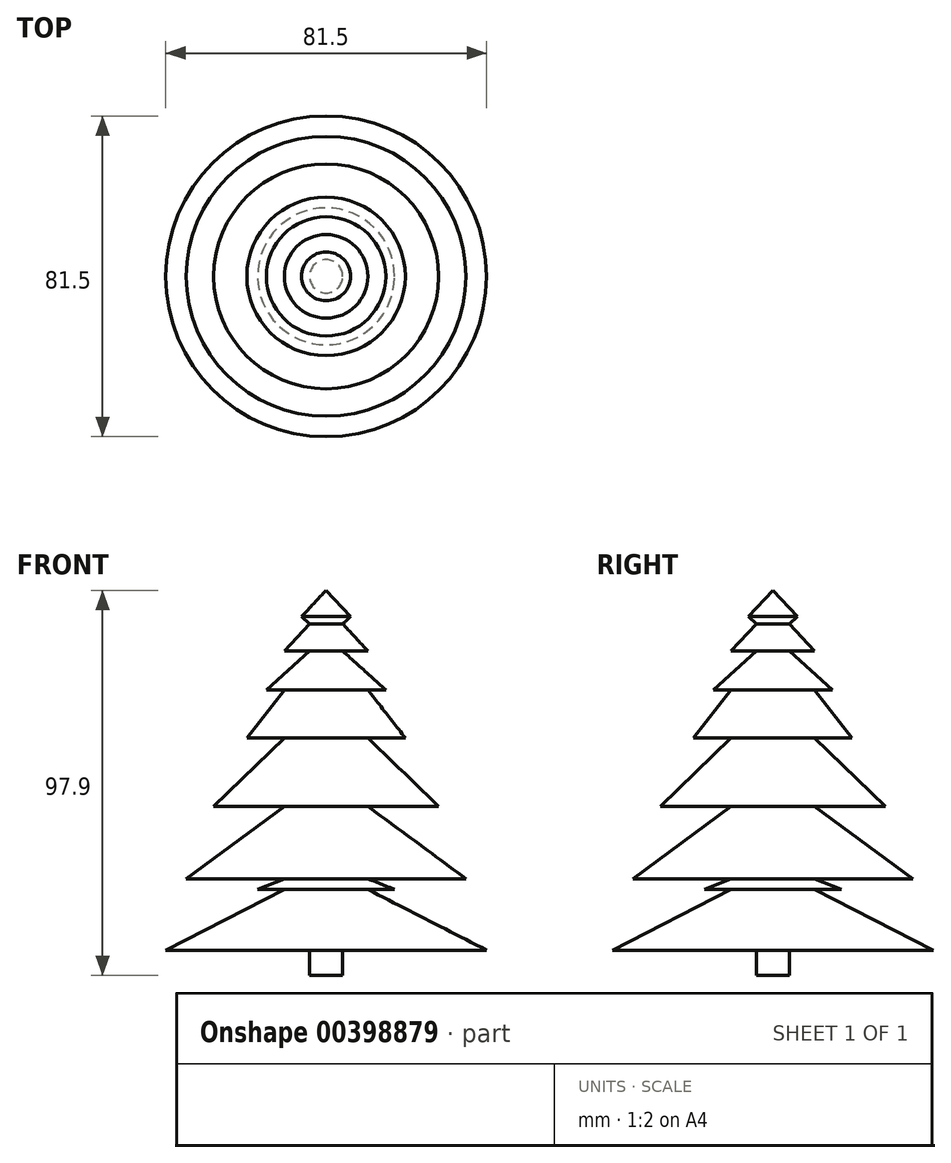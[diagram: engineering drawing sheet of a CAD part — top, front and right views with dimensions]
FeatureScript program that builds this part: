
annotation { "Feature Type Name" : "Feature", "Feature Type Description" : "" }
export const myFeature = defineFeature(function(context is Context, id is Id, definition is map)
    precondition{}
    {
        {
            var Q0;
            Q0=qCreatedBy(makeId("Front.planeOp"),FACE);
            var sketch = newSketch(context, id + "F0", { "sketchPlane" : qUnion([Q0])});
            skLineSegment(sketch, "E0", {"start": v(0, 59.14) * mm, "end": v(6.21, 52.43) * mm});
            skLineSegment(sketch, "E1", {"start": v(6.21, 52.43) * mm, "end": v(4.23, 50.59) * mm});
            skLineSegment(sketch, "E2", {"start": v(4.23, 50.59) * mm, "end": v(10.62, 43.69) * mm});
            skLineSegment(sketch, "E3", {"start": v(10.62, 43.69) * mm, "end": v(4.23, 43.69) * mm});
            skLineSegment(sketch, "E4", {"start": v(4.23, 43.69) * mm, "end": v(15.16, 33.8) * mm});
            skLineSegment(sketch, "E5", {"start": v(15.16, 33.8) * mm, "end": v(10.62, 33.8) * mm});
            skLineSegment(sketch, "E6", {"start": v(10.62, 33.8) * mm, "end": v(20.13, 21.62) * mm});
            skLineSegment(sketch, "E7", {"start": v(20.13, 21.62) * mm, "end": v(10.62, 21.62) * mm});
            skLineSegment(sketch, "E8", {"start": v(10.62, 21.62) * mm, "end": v(28.57, 4.22) * mm});
            skLineSegment(sketch, "E9", {"start": v(28.57, 4.22) * mm, "end": v(10.62, 4.22) * mm});
            skLineSegment(sketch, "E10", {"start": v(10.62, 4.22) * mm, "end": v(35.53, -14.16) * mm});
            skLineSegment(sketch, "E11", {"start": v(35.53, -14.16) * mm, "end": v(10.62, -14.16) * mm});
            skLineSegment(sketch, "E12", {"start": v(10.62, -14.16) * mm, "end": v(17.4, -16.9) * mm});
            skLineSegment(sketch, "E13", {"start": v(17.4, -16.9) * mm, "end": v(10.62, -16.9) * mm});
            skLineSegment(sketch, "E14", {"start": v(10.62, -16.9) * mm, "end": v(40.75, -32.3) * mm});
            skLineSegment(sketch, "E15", {"start": v(40.75, -32.3) * mm, "end": v(4.23, -32.3) * mm});
            skLineSegment(sketch, "E16", {"start": v(4.23, -32.3) * mm, "end": v(4.23, -38.76) * mm});
            skLineSegment(sketch, "E17", {"start": v(4.23, -38.76) * mm, "end": v(0, -38.76) * mm});
            skLineSegment(sketch, "E18", {"start": v(0, 59.14) * mm, "end": v(0, -38.76) * mm});
            skSolve(sketch);
        }
        {
            var Q0;
            Q0=makeQuery(id+"F0.imprint","IMPRINT",FACE,{"disambiguationData":[TD([[makeQuery(id+"F0.imprint","IMPRINT",EDGE,{"derivedFrom":sQuery(id+"F0.wireOp",EDGE,"E0")}),-1.0]])]});
            var Q1;
            Q1=sQuery(id+"F0.wireOp",EDGE,"E18");
            revolve(context, id + "F1", {"entities" : qUnion([Q0]), "axis" : qUnion([Q1]), "revolveType" : RevolveType.FULL});
        }
    });
